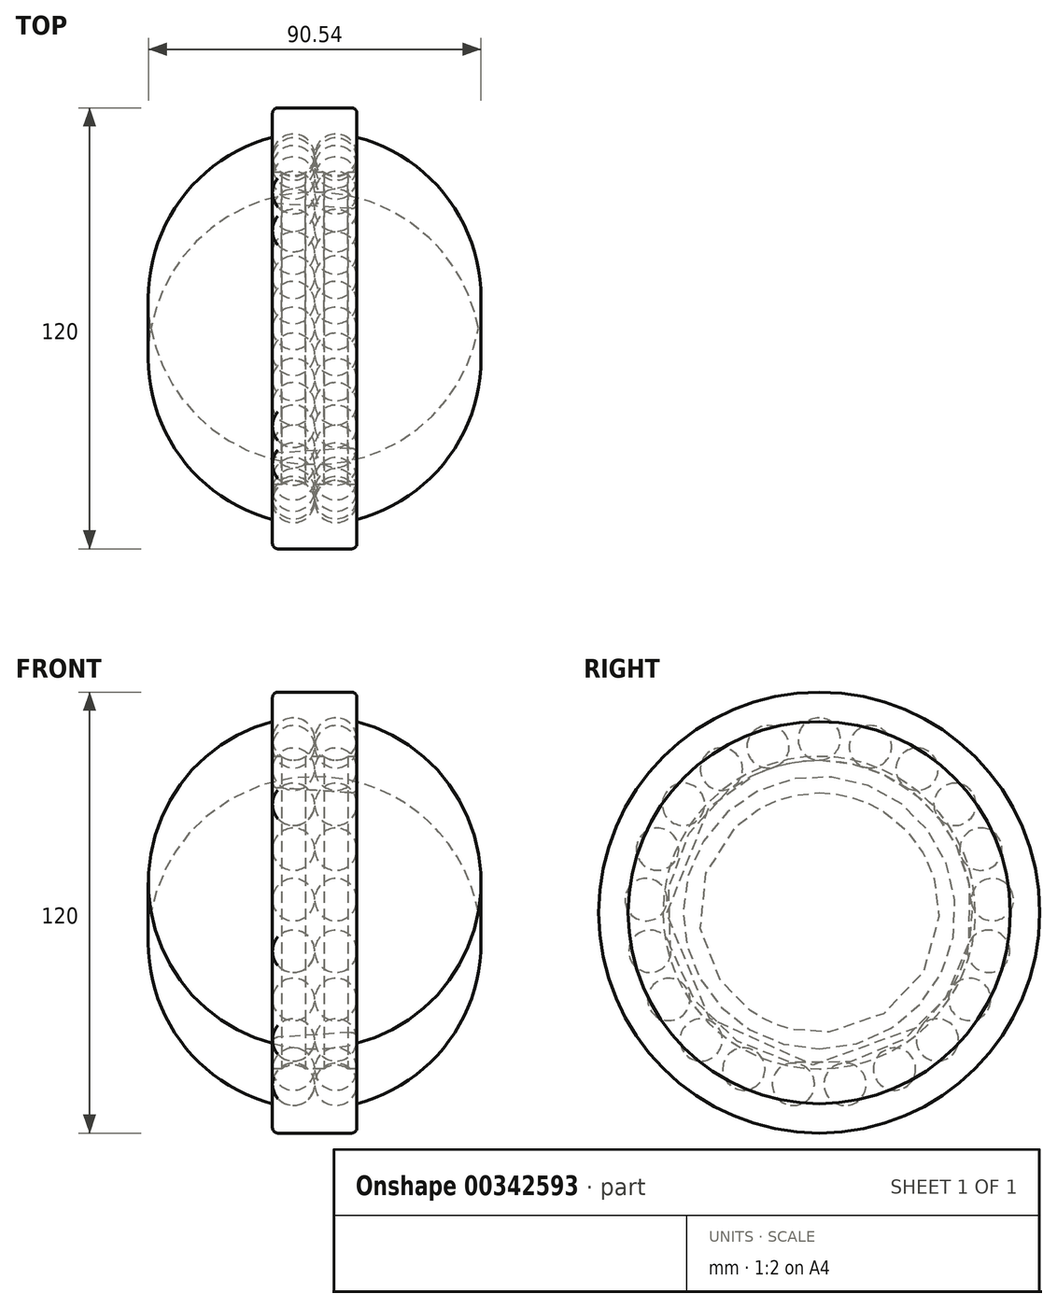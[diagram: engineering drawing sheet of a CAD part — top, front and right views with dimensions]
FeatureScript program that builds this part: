
annotation { "Feature Type Name" : "Feature", "Feature Type Description" : "" }
export const myFeature = defineFeature(function(context is Context, id is Id, definition is map)
    precondition{}
    {
        {
            var Q0;
            Q0=qCreatedBy(makeId("Front.planeOp"),FACE);
            var sketch = newSketch(context, id + "F0", { "sketchPlane" : qUnion([Q0])});
            skLineSegment(sketch, "E0", {"start": v(0, 0) * mm, "end": v(11.5, 0) * mm});
            skLineSegment(sketch, "E1", {"start": v(-10.1, 33.93) * mm, "end": v(9.9, 32.6) * mm});
            skLineSegment(sketch, "E2", {"start": v(11.5, 34.1) * mm, "end": v(11.5, 42.5) * mm});
            skLineSegment(sketch, "E3", {"start": v(11.5, 42.5) * mm, "end": v(9, 42.5) * mm});
            skLineSegment(sketch, "E4", {"start": v(-11.5, 42.5) * mm, "end": v(-11.5, 35.43) * mm});
            skPoint(sketch, "E5.visualSharp", {"position": v(-11.5, 34.02) * mm});
            skArc(sketch, "E5.filletArc", {"start": v(-11.5, 35.43) * mm, "mid": v(-11.1, 34.4) * mm, "end": v(-10.1, 33.93) * mm});
            skPoint(sketch, "E6.visualSharp", {"position": v(11.5, 32.5) * mm});
            skArc(sketch, "E6.filletArc", {"start": v(9.9, 32.6) * mm, "mid": v(11.02, 33) * mm, "end": v(11.5, 34.1) * mm});
            skLineSegment(sketch, "E7", {"start": v(11.5, 0) * mm, "end": v(11.5, 42.5) * mm});
            skLineSegment(sketch, "E8", {"start": v(11.5, 52) * mm, "end": v(11.5, 58.5) * mm});
            skLineSegment(sketch, "E9", {"start": v(10, 60) * mm, "end": v(-10, 60) * mm});
            skLineSegment(sketch, "E10", {"start": v(-11.5, 58.5) * mm, "end": v(-11.5, 52) * mm});
            skLineSegment(sketch, "E11", {"start": v(5.75, 53) * mm, "end": v(5.75, 41.5) * mm});
            skArc(sketch, "E12", {"start": v(2.5, 42.5) * mm, "mid": v(11.24, 45.55) * mm, "end": v(5.75, 53) * mm});
            skArc(sketch, "E13.MirrorC", {"start": v(-5.75, 53) * mm, "mid": v(-0.26, 45.55) * mm, "end": v(-9, 42.5) * mm});
            skLineSegment(sketch, "E14.MirrorCS", {"start": v(-5.75, 52) * mm, "end": v(-5.75, 47.25) * mm});
            skLineSegment(sketch, "E15.MirrorCS", {"start": v(-5.75, 53) * mm, "end": v(-5.75, 52) * mm});
            skPoint(sketch, "E16.orphan", {"position": v(-5.75, 52) * mm});
            skPoint(sketch, "E17.orphan", {"position": v(-5.75, 42.5) * mm});
            skPoint(sketch, "E18.orphan", {"position": v(5.75, 42.5) * mm});
            skPoint(sketch, "E19.orphan", {"position": v(5.75, 52) * mm});
            skLineSegment(sketch, "E20.trimOffspring", {"start": v(-9, 42.5) * mm, "end": v(-11.5, 42.5) * mm});
            skLineSegment(sketch, "E21.trimOffspring", {"start": v(2.5, 42.5) * mm, "end": v(-2.5, 42.5) * mm});
            skPoint(sketch, "E22.visualSharp", {"position": v(-11.5, 60) * mm});
            skArc(sketch, "E22.filletArc", {"start": v(-10, 60) * mm, "mid": v(-11.06, 59.56) * mm, "end": v(-11.5, 58.5) * mm});
            skPoint(sketch, "E23.visualSharp", {"position": v(11.5, 60) * mm});
            skArc(sketch, "E23.filletArc", {"start": v(11.5, 58.5) * mm, "mid": v(11.06, 59.56) * mm, "end": v(10, 60) * mm});
            skArc(sketch, "E24", {"start": v(11.5, 52) * mm, "mid": v(0, 53.48) * mm, "end": v(-11.5, 52) * mm});
            skLineSegment(sketch, "E25.trimOffspring", {"start": v(-5.75, 47.25) * mm, "end": v(-5.75, 41.5) * mm});
            skSolve(sketch);
        }
        {
            var Q0;
            Q0=makeQuery(id+"F0.imprint","IMPRINT",FACE,{"disambiguationData":[TD([[makeQuery(id+"F0.imprint","IMPRINT",EDGE,{"derivedFrom":sQuery(id+"F0.wireOp",EDGE,"E8")}),1.0]])]});
            var Q1;
            Q1=makeQuery(id+"F0.imprint","IMPRINT",FACE,{"disambiguationData":[TD([[makeQuery(id+"F0.imprint","IMPRINT",EDGE,{"derivedFrom":sQuery(id+"F0.wireOp",EDGE,"E1")}),1.0]])]});
            var Q2;
            Q2=sQuery(id+"F0.wireOp",EDGE,"E0");
            revolve(context, id + "F1", {"entities" : qUnion([Q0, Q1]), "axis" : qUnion([Q2]), "revolveType" : RevolveType.FULL});
        }
        {
            var Q0;
            Q0=makeQuery(id+"F0.imprint","IMPRINT",FACE,{"disambiguationData":[TD([[makeQuery(id+"F0.imprint","IMPRINT",EDGE,{"derivedFrom":sQuery(id+"F0.wireOp",EDGE,"E14.MirrorCS")}),1.0]])]});
            var Q1;
            Q1=sQuery(id+"F0.wireOp",EDGE,"E14.MirrorCS");
            revolve(context, id + "F2", {"entities" : qUnion([Q0]), "axis" : qUnion([Q1]), "revolveType" : RevolveType.FULL});
        }
        {
            var Q0;
            {var subQ0=sQuery(id+"F0.wireOp",EDGE,"E11");Q0=makeQuery(id+"F0.imprint","IMPRINT",FACE,{"disambiguationData":[TD([[makeQuery(id+"F0.imprint","IMPRINT",EDGE,{"derivedFrom":subQ0}),1.0]])]});}
            var Q1;
            Q1=sQuery(id+"F0.wireOp",EDGE,"E11");
            revolve(context, id + "F3", {"entities" : qUnion([Q0]), "axis" : qUnion([Q1]), "revolveType" : RevolveType.FULL});
        }
        {
            var Q0;
            Q0=makeQuery(id+"F2.opRevolve","SWEPT_BODY",BODY,{"disambiguationData":[OSD([sQuery(id+"F0.wireOp",EDGE,"E13.MirrorC"),sQuery(id+"F0.wireOp",EDGE,"E14.MirrorCS"),sQuery(id+"F0.wireOp",EDGE,"E15.MirrorCS"),sQuery(id+"F0.wireOp",EDGE,"E25.trimOffspring")])]});
            var Q1;
            Q1=makeQuery(id+"F3.opRevolve","SWEPT_BODY",BODY,{"disambiguationData":[OSD([sQuery(id+"F0.wireOp",EDGE,"E11"),sQuery(id+"F0.wireOp",EDGE,"E12")])]});
            var Q2;
            Q2=sQuery(id+"F0.wireOp",EDGE,"E0");
            circularPattern(context, id + "F4", {"entities" : qUnion([Q0, Q1]), "axis" : qUnion([Q2]), "angle" : 360 * degree, "instanceCount" : 21, "equalSpace" : true});
        }
    });
